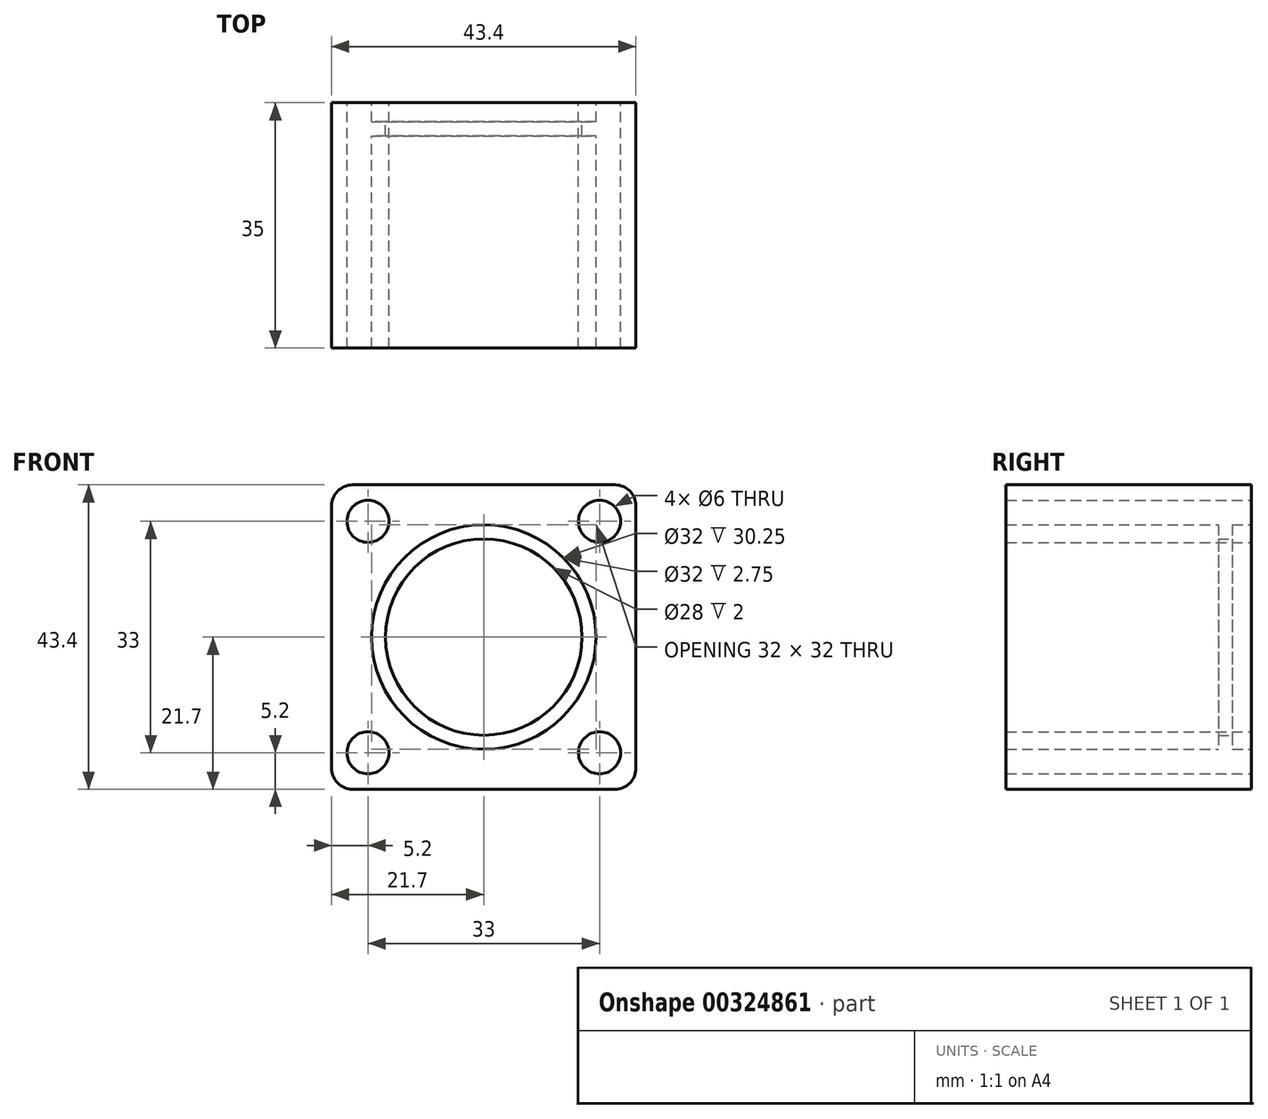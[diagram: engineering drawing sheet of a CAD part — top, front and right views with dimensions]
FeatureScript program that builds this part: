
annotation { "Feature Type Name" : "Feature", "Feature Type Description" : "" }
export const myFeature = defineFeature(function(context is Context, id is Id, definition is map)
    precondition{}
    {
        {
            var Q0;
            Q0=qCreatedBy(makeId("Front.planeOp"),FACE);
            var sketch = newSketch(context, id + "F0", { "sketchPlane" : qUnion([Q0])});
            skLineSegment(sketch, "E0.bottom", {"start": v(-21.7, 21.7) * mm, "end": v(21.7, 21.7) * mm});
            skLineSegment(sketch, "E0.top", {"start": v(-21.7, -21.7) * mm, "end": v(21.7, -21.7) * mm});
            skLineSegment(sketch, "E0.left", {"start": v(-21.7, 21.7) * mm, "end": v(-21.7, -21.7) * mm});
            skLineSegment(sketch, "E0.right", {"start": v(21.7, 21.7) * mm, "end": v(21.7, -21.7) * mm});
            skPoint(sketch, "E0.middle", {"position": v(0, 0) * mm});
            skCircle(sketch, "E1", {"center": v(0, 0) * mm, "radius": 16 * mm});
            skLineSegment(sketch, "E2", {"start": v(-21.7, 21.7) * mm, "end": v(21.7, -21.7) * mm, "construction": true});
            skLineSegment(sketch, "E3", {"start": v(-21.7, -21.7) * mm, "end": v(21.7, 21.7) * mm, "construction": true});
            skLineSegment(sketch, "E4.bottom", {"start": v(-16.5, 16.5) * mm, "end": v(16.5, 16.5) * mm, "construction": true});
            skLineSegment(sketch, "E4.top", {"start": v(-16.5, -16.5) * mm, "end": v(16.5, -16.5) * mm, "construction": true});
            skLineSegment(sketch, "E4.left", {"start": v(-16.5, 16.5) * mm, "end": v(-16.5, -16.5) * mm, "construction": true});
            skLineSegment(sketch, "E4.right", {"start": v(16.5, 16.5) * mm, "end": v(16.5, -16.5) * mm, "construction": true});
            skCircle(sketch, "E5", {"center": v(-16.5, 16.5) * mm, "radius": 3 * mm});
            skCircle(sketch, "E6", {"center": v(16.5, 16.5) * mm, "radius": 3 * mm});
            skCircle(sketch, "E7", {"center": v(-16.5, -16.5) * mm, "radius": 3 * mm});
            skCircle(sketch, "E8", {"center": v(16.5, -16.5) * mm, "radius": 3 * mm});
            skSolve(sketch);
        }
        {
            var Q0;
            Q0=makeQuery(id+"F0.imprint","IMPRINT",FACE,{"disambiguationData":[TD([[makeQuery(id+"F0.imprint","IMPRINT",EDGE,{"derivedFrom":sQuery(id+"F0.wireOp",EDGE,"E0.bottom")}),-1.0]])]});
            extrude(context, id + "F1", {"entities" : qUnion([Q0]), "depth" : 35 * mm, "symmetric" : true});
        }
        {
            var Q0;
            Q0=makeQuery(id+"F1.opExtrude","CAP_FACE",FACE,{"disambiguationData":[OSD([sQuery(id+"F0.wireOp",EDGE,"E0.bottom"),sQuery(id+"F0.wireOp",EDGE,"E0.top"),sQuery(id+"F0.wireOp",EDGE,"E0.left"),sQuery(id+"F0.wireOp",EDGE,"E0.right"),sQuery(id+"F0.wireOp",EDGE,"E1"),sQuery(id+"F0.wireOp",EDGE,"E5"),sQuery(id+"F0.wireOp",EDGE,"E6"),sQuery(id+"F0.wireOp",EDGE,"E7"),sQuery(id+"F0.wireOp",EDGE,"E8")])],"isStart":true});
            cPlane(context, id + "F2", {"entities" : qUnion([Q0]), "cplaneType" : CPlaneType.OFFSET, "offset" : 2.75 * mm, "oppositeDirection" : true, "width" : 150 * mm, "height" : 150 * mm});
        }
        {
            var Q0;
            Q0=qCreatedBy(id+"F2.planeOp",FACE);
            var sketch = newSketch(context, id + "F3", { "sketchPlane" : qUnion([Q0])});
            skCircle(sketch, "E9.0", {"center": v(0, 0) * mm, "radius": 16 * mm});
            skCircle(sketch, "E10", {"center": v(0, 0) * mm, "radius": 14 * mm});
            skSolve(sketch);
        }
        {
            var Q0;
            Q0=makeQuery(id+"F3.imprint","IMPRINT",FACE,{"disambiguationData":[TD([[makeQuery(id+"F3.imprint","IMPRINT",EDGE,{"derivedFrom":sQuery(id+"F3.wireOp",EDGE,"E9.0")}),1.0]])]});
            extrude(context, id + "F4", {"entities" : qUnion([Q0]), "operationType" : NewBodyOperationType.ADD, "oppositeDirection" : true, "depth" : 2 * mm});
        }
        {
            var Q0;
            Q0=makeQuery(id+"F1.opExtrude","SWEPT_EDGE",EDGE,{"disambiguationData":[OSD([sQuery(id+"F0.wireOp",EDGE,"E0.bottom"),sQuery(id+"F0.wireOp",EDGE,"E0.left")])]});
            var Q1;
            Q1=makeQuery(id+"F1.opExtrude","SWEPT_EDGE",EDGE,{"disambiguationData":[OSD([sQuery(id+"F0.wireOp",EDGE,"E0.bottom"),sQuery(id+"F0.wireOp",EDGE,"E0.right")])]});
            var Q2;
            Q2=makeQuery(id+"F1.opExtrude","SWEPT_EDGE",EDGE,{"disambiguationData":[OSD([sQuery(id+"F0.wireOp",EDGE,"E0.top"),sQuery(id+"F0.wireOp",EDGE,"E0.right")])]});
            var Q3;
            Q3=makeQuery(id+"F1.opExtrude","SWEPT_EDGE",EDGE,{"disambiguationData":[OSD([sQuery(id+"F0.wireOp",EDGE,"E0.top"),sQuery(id+"F0.wireOp",EDGE,"E0.left")])]});
            fillet(context, id + "F5", {"entities" : qUnion([Q0, Q1, Q2, Q3]), "radius" : 3 * mm, "tangentPropagation" : true, "allowEdgeOverflow" : false});
        }
    });
